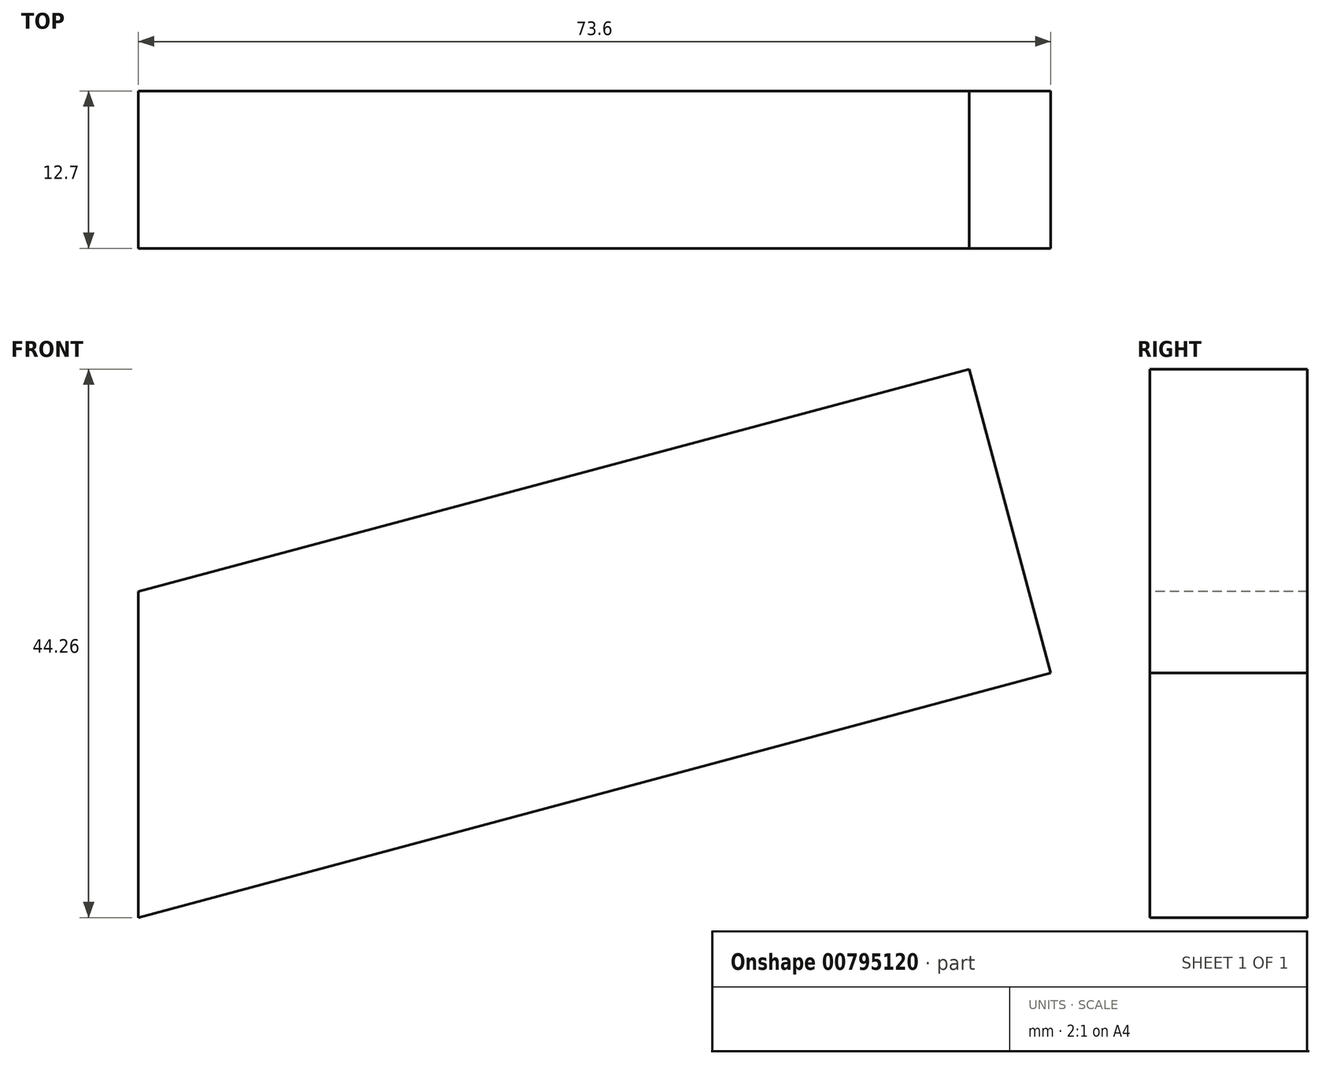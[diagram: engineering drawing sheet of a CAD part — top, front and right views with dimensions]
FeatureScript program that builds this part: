
annotation { "Feature Type Name" : "Feature", "Feature Type Description" : "" }
export const myFeature = defineFeature(function(context is Context, id is Id, definition is map)
    precondition{}
    {
        {
            var Q0;
            Q0=qCreatedBy(makeId("Front.planeOp"),FACE);
            var sketch = newSketch(context, id + "F0", { "sketchPlane" : qUnion([Q0])});
            skLineSegment(sketch, "E0", {"start": v(0, 0) * mm, "end": v(0, 75.75) * mm, "construction": true});
            skLineSegment(sketch, "E1", {"start": v(0, 26.3) * mm, "end": v(67.03, 44.26) * mm});
            skLineSegment(sketch, "E2", {"start": v(0, 0) * mm, "end": v(73.6, 19.72) * mm});
            skLineSegment(sketch, "E3", {"start": v(73.6, 19.72) * mm, "end": v(67.03, 44.26) * mm});
            skLineSegment(sketch, "E4", {"start": v(0, 0) * mm, "end": v(0, 26.3) * mm});
            skSolve(sketch);
        }
        {
            var Q0;
            Q0=makeQuery(id+"F0.imprint","IMPRINT",FACE,{"disambiguationData":[TD([[makeQuery(id+"F0.imprint","IMPRINT",EDGE,{"derivedFrom":sQuery(id+"F0.wireOp",EDGE,"E1")}),-1.0]])]});
            extrude(context, id + "F1", {"entities" : qUnion([Q0]), "endBound" : BoundingType.SYMMETRIC, "oppositeDirection" : true, "depth" : 12.7 * mm, "offsetDistance" : 25 * mm});
        }
    });
